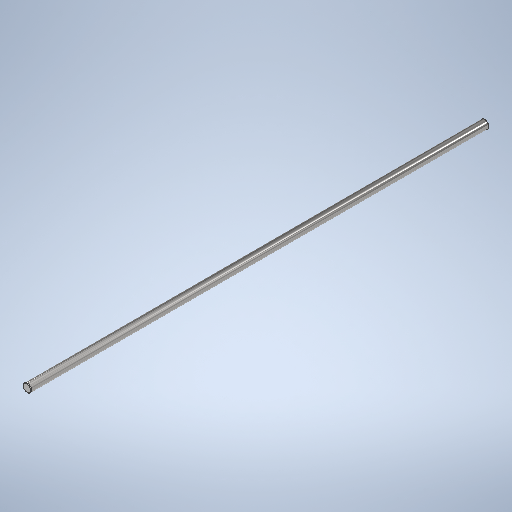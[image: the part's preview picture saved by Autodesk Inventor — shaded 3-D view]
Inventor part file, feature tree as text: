
AUTODESK INVENTOR PART (.ipt)
format: ipt  version: 2025.2 (Build 292293000, 293)  size: 253,440 bytes
history: native  units: mm
features: extrude x1, chamfer x1, sketch x1
ambient origin geometry x8: Origin, YZ Plane, XZ Plane, XY Plane, X Axis, Y Axis, Z Axis, Center Point
bodies: Solid1 (feature_tree)
feature tree (3):
  extrude  "Extrusion1"  Depth=444.0mm TaperAngle=0.0deg
  chamfer  "Chamfer1"  Distance=0.5mm Angle=45.0deg
  sketch  "Sketch1"  dims[d0=8.0mm d1=444.0mm d2=0.0mm d3=0.5mm d4=2.0mm d5=45.0deg]
